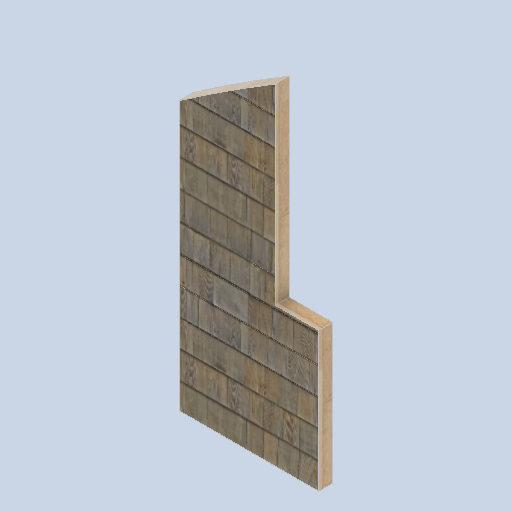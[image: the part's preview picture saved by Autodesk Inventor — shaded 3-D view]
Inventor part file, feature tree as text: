
AUTODESK INVENTOR PART (.ipt)
format: ipt  version: 2024.2 (Build 282272000, 272)  size: 372,224 bytes
history: native  units: mm
features: extrude x1, sketch x1
ambient origin geometry x8: Origin, YZ Plane, XZ Plane, XY Plane, X Axis, Y Axis, Z Axis, Center Point
bodies: Solid1 (feature_tree)
feature tree (2):
  extrude  "Extrusion1"  [1 undecoded]
  sketch  "Sketch1"  dims[d0=80.0mm d1=0.0mm]
note: 1 required parameter value undecoded (feature->parameter linkage not recoverable at this tier; creation-order binding heuristic only, values carry confidence <= 0.55)
